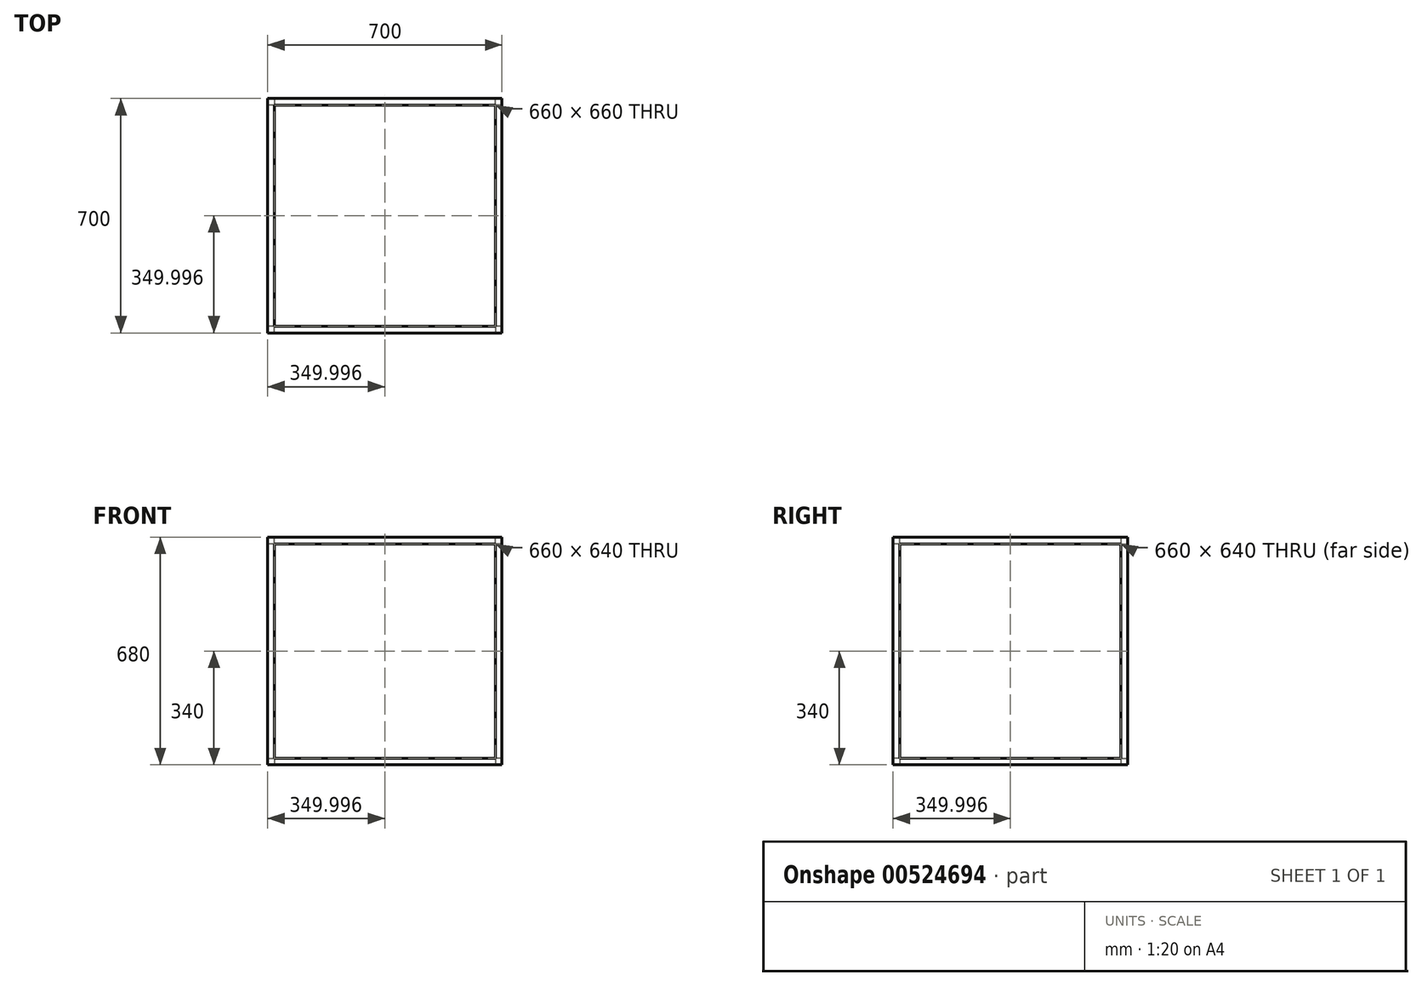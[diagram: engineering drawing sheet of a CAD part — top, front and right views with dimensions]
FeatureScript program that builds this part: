
annotation { "Feature Type Name" : "Feature", "Feature Type Description" : "" }
export const myFeature = defineFeature(function(context is Context, id is Id, definition is map)
    precondition{}
    {
        {
            var Q0;
            Q0=qCreatedBy(makeId("Top.planeOp"),FACE);
            var sketch = newSketch(context, id + "F0", { "sketchPlane" : qUnion([Q0])});
            skLineSegment(sketch, "E0.bottom", {"start": v(-349.06, 480.52) * mm, "end": v(350.94, 480.52) * mm});
            skLineSegment(sketch, "E0.top", {"start": v(-349.06, -219.48) * mm, "end": v(350.94, -219.48) * mm});
            skLineSegment(sketch, "E0.left", {"start": v(-349.06, 480.52) * mm, "end": v(-349.06, -219.48) * mm});
            skLineSegment(sketch, "E0.right", {"start": v(350.94, 480.52) * mm, "end": v(350.94, -219.48) * mm});
            skLineSegment(sketch, "E1.bottom", {"start": v(-329.06, -199.48) * mm, "end": v(330.94, -199.48) * mm});
            skLineSegment(sketch, "E1.top", {"start": v(-329.06, 460.52) * mm, "end": v(330.94, 460.52) * mm});
            skLineSegment(sketch, "E1.left", {"start": v(-329.06, -199.48) * mm, "end": v(-329.06, 460.52) * mm});
            skLineSegment(sketch, "E1.right", {"start": v(330.94, -199.48) * mm, "end": v(330.94, 460.52) * mm});
            skLineSegment(sketch, "E2", {"start": v(-329.06, 460.52) * mm, "end": v(-349.06, 460.52) * mm});
            skLineSegment(sketch, "E3", {"start": v(-329.06, 460.52) * mm, "end": v(-329.06, 480.52) * mm});
            skLineSegment(sketch, "E4", {"start": v(-329.06, -199.48) * mm, "end": v(-329.06, -219.48) * mm});
            skLineSegment(sketch, "E5", {"start": v(-329.06, -199.48) * mm, "end": v(-349.06, -199.48) * mm});
            skSolve(sketch);
        }
        {
            var Q0;
            {var subQ0=sQuery(id+"F0.wireOp",EDGE,"E0.right");Q0=makeQuery(id+"F0.imprint","IMPRINT",FACE,{"disambiguationData":[TD([[makeQuery(id+"F0.imprint","IMPRINT",EDGE,{"derivedFrom":subQ0}),-1.0]])]});}
            var Q1;
            Q1=makeQuery(id+"F0.imprint","IMPRINT",FACE,{"disambiguationData":[TD([[makeQuery(id+"F0.imprint","IMPRINT",EDGE,{"derivedFrom":sQuery(id+"F0.wireOp",EDGE,"E1.left")}),1.0]])]});
            var Q2;
            {var subQ4=sQuery(id+"F0.wireOp",EDGE,"E2");Q2=makeQuery(id+"F0.imprint","IMPRINT",FACE,{"disambiguationData":[TD([[makeQuery(id+"F0.imprint","IMPRINT",EDGE,{"derivedFrom":subQ4}),-1.0]])]});}
            var Q3;
            {var subQ3=sQuery(id+"F0.wireOp",EDGE,"E4");Q3=makeQuery(id+"F0.imprint","IMPRINT",FACE,{"disambiguationData":[TD([[makeQuery(id+"F0.imprint","IMPRINT",EDGE,{"derivedFrom":subQ3}),-1.0]])]});}
            extrude(context, id + "F1", {"entities" : qUnion([Q0, Q1, Q2, Q3]), "depth" : 20 * mm, "offsetDistance" : 25 * mm});
        }
        {
            var Q0;
            {var subQ4=sQuery(id+"F0.wireOp",EDGE,"E2");Q0=makeQuery(id+"F0.imprint","IMPRINT",FACE,{"disambiguationData":[TD([[makeQuery(id+"F0.imprint","IMPRINT",EDGE,{"derivedFrom":subQ4}),-1.0]])]});}
            var Q1;
            {var subQ3=sQuery(id+"F0.wireOp",EDGE,"E4");Q1=makeQuery(id+"F0.imprint","IMPRINT",FACE,{"disambiguationData":[TD([[makeQuery(id+"F0.imprint","IMPRINT",EDGE,{"derivedFrom":subQ3}),-1.0]])]});}
            extrude(context, id + "F2", {"entities" : qUnion([Q0, Q1]), "operationType" : NewBodyOperationType.ADD, "depth" : 680 * mm, "offsetDistance" : 25 * mm});
        }
        {
            var Q0;
            Q0=makeQuery(id+"F2.opExtrude","SWEPT_FACE",FACE,{"disambiguationData":[OSD([sQuery(id+"F0.wireOp",EDGE,"E5")])]});
            var sketch = newSketch(context, id + "F3", { "sketchPlane" : qUnion([Q0])});
            skLineSegment(sketch, "E6", {"start": v(329.06, 660) * mm, "end": v(349.06, 660) * mm});
            skSolve(sketch);
        }
        {
            var Q0;
            {var subQ0=sQuery(id+"F3.wireOp",EDGE,"E6");Q0=makeQuery(id+"F3.imprint","IMPRINT",FACE,{"disambiguationData":[TD([[makeQuery(id+"F3.imprint","IMPRINT",EDGE,{"derivedFrom":subQ0}),1.0]])]});}
            extrude(context, id + "F4", {"entities" : qUnion([Q0]), "operationType" : NewBodyOperationType.ADD, "depth" : 660 * mm, "offsetDistance" : 25 * mm});
        }
        {
            var Q0;
            {var subQ0=sQuery(id+"F0.wireOp",EDGE,"E4");Q0=makeQuery(id+"F4.boolean.opBoolean","MERGE",FACE,{"derivedFrom":[makeQuery(id+"F2.opExtrude","SWEPT_FACE",FACE,{"disambiguationData":[OSD([sQuery(id+"F0.wireOp",EDGE,"E3")])]}),makeQuery(id+"F2.opExtrude","SWEPT_FACE",FACE,{"disambiguationData":[OSD([subQ0])]}),makeQuery(id+"F4.opExtrude","SWEPT_FACE",FACE,{"disambiguationData":[OSD([sQuery(id+"F0.wireOp",EDGE,"E1.bottom"),sQuery(id+"F0.wireOp",EDGE,"E1.left"),subQ0,sQuery(id+"F0.wireOp",EDGE,"E5")])]})]});}
            var sketch = newSketch(context, id + "F5", { "sketchPlane" : qUnion([Q0])});
            skLineSegment(sketch, "E7", {"start": v(-199.48, 660) * mm, "end": v(-219.48, 660) * mm});
            skLineSegment(sketch, "E8", {"start": v(-199.48, 660) * mm, "end": v(-199.48, 680) * mm});
            skLineSegment(sketch, "E9", {"start": v(460.52, 660) * mm, "end": v(480.52, 660) * mm});
            skLineSegment(sketch, "E10", {"start": v(460.52, 680) * mm, "end": v(460.52, 660) * mm});
            skSolve(sketch);
        }
        {
            var Q0;
            {var subQ0=sQuery(id+"F5.wireOp",EDGE,"E7");Q0=makeQuery(id+"F5.imprint","IMPRINT",FACE,{"disambiguationData":[TD([[makeQuery(id+"F5.imprint","IMPRINT",EDGE,{"derivedFrom":subQ0}),-1.0]])]});}
            var Q1;
            {var subQ0=sQuery(id+"F5.wireOp",EDGE,"E9");Q1=makeQuery(id+"F5.imprint","IMPRINT",FACE,{"disambiguationData":[TD([[makeQuery(id+"F5.imprint","IMPRINT",EDGE,{"derivedFrom":subQ0}),1.0]])]});}
            extrude(context, id + "F6", {"entities" : qUnion([Q0, Q1]), "operationType" : NewBodyOperationType.ADD, "depth" : 680 * mm, "offsetDistance" : 25 * mm});
        }
        {
            var Q0;
            {var subQ0=sQuery(id+"F0.wireOp",EDGE,"E0.bottom");var subQ1=sQuery(id+"F0.wireOp",EDGE,"E1.right");var subQ2=sQuery(id+"F0.wireOp",EDGE,"E1.left");var subQ3=sQuery(id+"F0.wireOp",EDGE,"E0.top");var subQ4=sQuery(id+"F0.wireOp",EDGE,"E1.top");var subQ5=sQuery(id+"F0.wireOp",EDGE,"E1.bottom");var subQ6=sQuery(id+"F0.wireOp",EDGE,"E0.right");var subQ7=makeQuery(id+"F1.opExtrude","CAP_FACE",FACE,{"disambiguationData":[OSD([subQ0,subQ3,sQuery(id+"F0.wireOp",EDGE,"E0.left"),subQ6,subQ5,subQ4,subQ2,subQ1])],"isStart":false});Q0=makeQuery(id+"F2.boolean.opBoolean","SPLIT",FACE,{"disambiguationData":[TD([makeQuery(id+"F1.opExtrude","SWEPT_FACE",FACE,{"disambiguationData":[OSD([subQ0])]})])],"derivedFrom":subQ7});}
            var sketch = newSketch(context, id + "F7", { "sketchPlane" : qUnion([Q0])});
            skLineSegment(sketch, "E11", {"start": v(350.94, 460.52) * mm, "end": v(330.94, 460.52) * mm});
            skLineSegment(sketch, "E12", {"start": v(330.94, 460.52) * mm, "end": v(330.94, 480.52) * mm});
            skLineSegment(sketch, "E13", {"start": v(350.94, -199.48) * mm, "end": v(330.94, -199.48) * mm});
            skLineSegment(sketch, "E14", {"start": v(330.94, -199.48) * mm, "end": v(330.94, -219.48) * mm});
            skSolve(sketch);
        }
        {
            var Q0;
            {var subQ0=sQuery(id+"F7.wireOp",EDGE,"E11");Q0=makeQuery(id+"F7.imprint","IMPRINT",FACE,{"disambiguationData":[TD([[makeQuery(id+"F7.imprint","IMPRINT",EDGE,{"derivedFrom":subQ0}),-1.0]])]});}
            var Q1;
            {var subQ0=sQuery(id+"F7.wireOp",EDGE,"E13");Q1=makeQuery(id+"F7.imprint","IMPRINT",FACE,{"disambiguationData":[TD([[makeQuery(id+"F7.imprint","IMPRINT",EDGE,{"derivedFrom":subQ0}),1.0]])]});}
            extrude(context, id + "F8", {"entities" : qUnion([Q0, Q1]), "operationType" : NewBodyOperationType.ADD, "depth" : 660 * mm, "offsetDistance" : 25 * mm});
        }
        {
            var Q0;
            Q0=makeQuery(id+"F8.boolean.opBoolean","MERGE",FACE,{"derivedFrom":[makeQuery(id+"F6.opExtrude","SWEPT_FACE",FACE,{"disambiguationData":[OSD([sQuery(id+"F5.wireOp",EDGE,"E10")])]}),makeQuery(id+"F8.opExtrude","SWEPT_FACE",FACE,{"disambiguationData":[OSD([sQuery(id+"F7.wireOp",EDGE,"E11")])]})]});
            var sketch = newSketch(context, id + "F9", { "sketchPlane" : qUnion([Q0])});
            skLineSegment(sketch, "E15", {"start": v(350.94, 660) * mm, "end": v(330.94, 660) * mm});
            skLineSegment(sketch, "E16", {"start": v(330.94, 660) * mm, "end": v(330.94, 680) * mm});
            skSolve(sketch);
        }
        {
            var Q0;
            {var subQ0=sQuery(id+"F9.wireOp",EDGE,"E15");Q0=makeQuery(id+"F9.imprint","IMPRINT",FACE,{"disambiguationData":[TD([[makeQuery(id+"F9.imprint","IMPRINT",EDGE,{"derivedFrom":subQ0}),-1.0]])]});}
            extrude(context, id + "F10", {"entities" : qUnion([Q0]), "operationType" : NewBodyOperationType.ADD, "depth" : 660 * mm, "offsetDistance" : 25 * mm});
        }
    });
